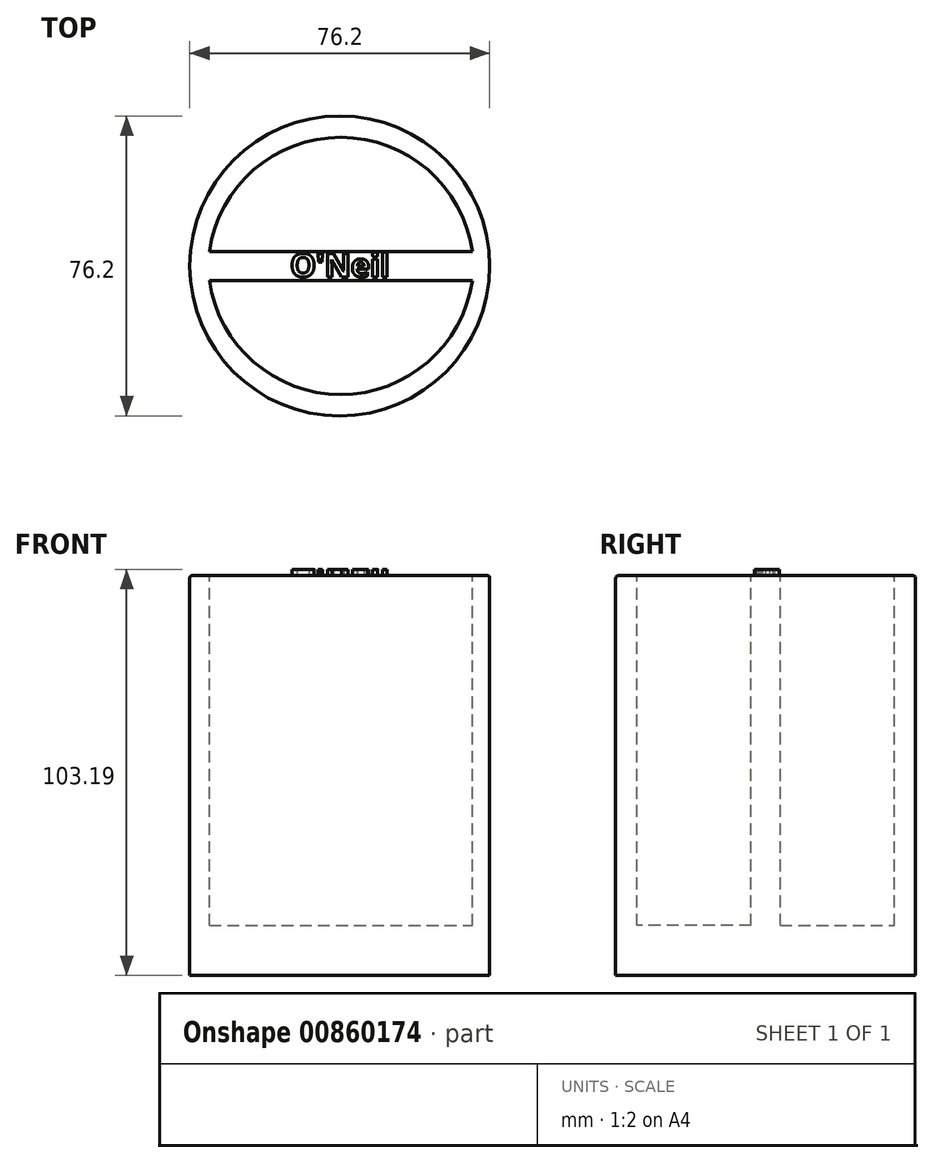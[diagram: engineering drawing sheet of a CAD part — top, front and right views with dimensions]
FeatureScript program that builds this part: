
annotation { "Feature Type Name" : "Feature", "Feature Type Description" : "" }
export const myFeature = defineFeature(function(context is Context, id is Id, definition is map)
    precondition{}
    {
        {
            var Q0;
            Q0=qCreatedBy(makeId("Top.planeOp"),FACE);
            var sketch = newSketch(context, id + "F0", { "sketchPlane" : qUnion([Q0])});
            skCircle(sketch, "E0", {"center": v(0, 0) * mm, "radius": 38.1 * mm});
            skSolve(sketch);
        }
        {
            var Q0;
            Q0=makeQuery(id+"F0.imprint","IMPRINT",FACE,{"disambiguationData":[TD([[makeQuery(id+"F0.imprint","IMPRINT",EDGE,{"derivedFrom":sQuery(id+"F0.wireOp",EDGE,"E0")}),1.0]])]});
            extrude(context, id + "F1", {"entities" : qUnion([Q0]), "depth" : 101.6 * mm, "offsetDistance" : 25.4 * mm});
        }
        {
            var Q0;
            Q0=makeQuery(id+"F1.opExtrude","CAP_FACE",FACE,{"disambiguationData":[OSD([sQuery(id+"F0.wireOp",EDGE,"E0")])],"isStart":false});
            var sketch = newSketch(context, id + "F2", { "sketchPlane" : qUnion([Q0])});
            skArc(sketch, "E1", {"start": v(33.66, 3.7) * mm, "mid": v(0.26, 32.68) * mm, "end": v(-33.14, 3.7) * mm});
            skLineSegment(sketch, "E2", {"start": v(-33.14, 3.7) * mm, "end": v(33.66, 3.7) * mm});
            skLineSegment(sketch, "E3", {"start": v(-12.7, 0) * mm, "end": v(24.29, 0) * mm, "construction": true});
            skLineSegment(sketch, "E4.MirrorCS", {"start": v(-33.14, -3.7) * mm, "end": v(33.66, -3.7) * mm});
            skArc(sketch, "E5.MirrorCS", {"start": v(33.66, -3.7) * mm, "mid": v(0.26, -32.68) * mm, "end": v(-33.14, -3.7) * mm});
            skSolve(sketch);
        }
        {
            var Q0;
            Q0=makeQuery(id+"F2.imprint","IMPRINT",FACE,{"disambiguationData":[TD([[makeQuery(id+"F2.imprint","IMPRINT",EDGE,{"derivedFrom":sQuery(id+"F2.wireOp",EDGE,"E1")}),1.0]])]});
            var Q1;
            Q1=makeQuery(id+"F2.imprint","IMPRINT",FACE,{"disambiguationData":[TD([[makeQuery(id+"F2.imprint","IMPRINT",EDGE,{"derivedFrom":sQuery(id+"F2.wireOp",EDGE,"E4.MirrorCS")}),-1.0]])]});
            extrude(context, id + "F3", {"entities" : qUnion([Q0, Q1]), "operationType" : NewBodyOperationType.REMOVE, "oppositeDirection" : true, "depth" : 88.9 * mm, "offsetDistance" : 25.4 * mm});
        }
        {
            var Q0;
            Q0=makeQuery(id+"F1.opExtrude","CAP_FACE",FACE,{"disambiguationData":[OSD([sQuery(id+"F0.wireOp",EDGE,"E0")])],"isStart":false});
            var sketch = newSketch(context, id + "F4", { "sketchPlane" : qUnion([Q0])});
            skText(sketch, "E6", { "text": "O\'Neil", "fontName": "OpenSans-Bold.ttf"});
            const initialGuessF4  = {"E6": [-0.0126, -0.00277, 1, 0, 0.00592]};
            skSetInitialGuess(sketch, initialGuessF4);
            skSolve(sketch);
        }
        {
            var Q0;
            Q0 = qSketchRegion(id + "F4", true);
            extrude(context, id + "F5", {"entities" : qUnion([Q0]), "operationType" : NewBodyOperationType.ADD, "depth" : 1.59 * mm, "offsetDistance" : 25.4 * mm});
        }
        {
            var Q0;
            Q0=makeQuery(id+"F3.boolean.opBoolean","COPY",EDGE,{"derivedFrom":makeQuery(id+"F3.opExtrude","CAP_EDGE",EDGE,{"disambiguationData":[OSD([sQuery(id+"F2.wireOp",EDGE,"E5.MirrorCS")])],"isStart":true})});
            var Q1;
            Q1=makeQuery(id+"F3.boolean.opBoolean","COPY",EDGE,{"derivedFrom":makeQuery(id+"F3.opExtrude","CAP_EDGE",EDGE,{"disambiguationData":[OSD([sQuery(id+"F2.wireOp",EDGE,"E4.MirrorCS")])],"isStart":true})});
            var Q2;
            Q2=makeQuery(id+"F3.boolean.opBoolean","COPY",EDGE,{"derivedFrom":makeQuery(id+"F3.opExtrude","CAP_EDGE",EDGE,{"disambiguationData":[OSD([sQuery(id+"F2.wireOp",EDGE,"E2")])],"isStart":true})});
            var Q3;
            Q3=makeQuery(id+"F3.boolean.opBoolean","COPY",EDGE,{"derivedFrom":makeQuery(id+"F3.opExtrude","CAP_EDGE",EDGE,{"disambiguationData":[OSD([sQuery(id+"F2.wireOp",EDGE,"E1")])],"isStart":true})});
            var Q4;
            Q4=makeQuery(id+"F1.opExtrude","CAP_EDGE",EDGE,{"disambiguationData":[OSD([sQuery(id+"F0.wireOp",EDGE,"E0")])],"isStart":false});
            fillet(context, id + "F6", {"entities" : qUnion([Q0, Q1, Q2, Q3, Q4]), "radius" : 0.64 * mm, "tangentPropagation" : true, "allowEdgeOverflow" : false});
        }
    });
